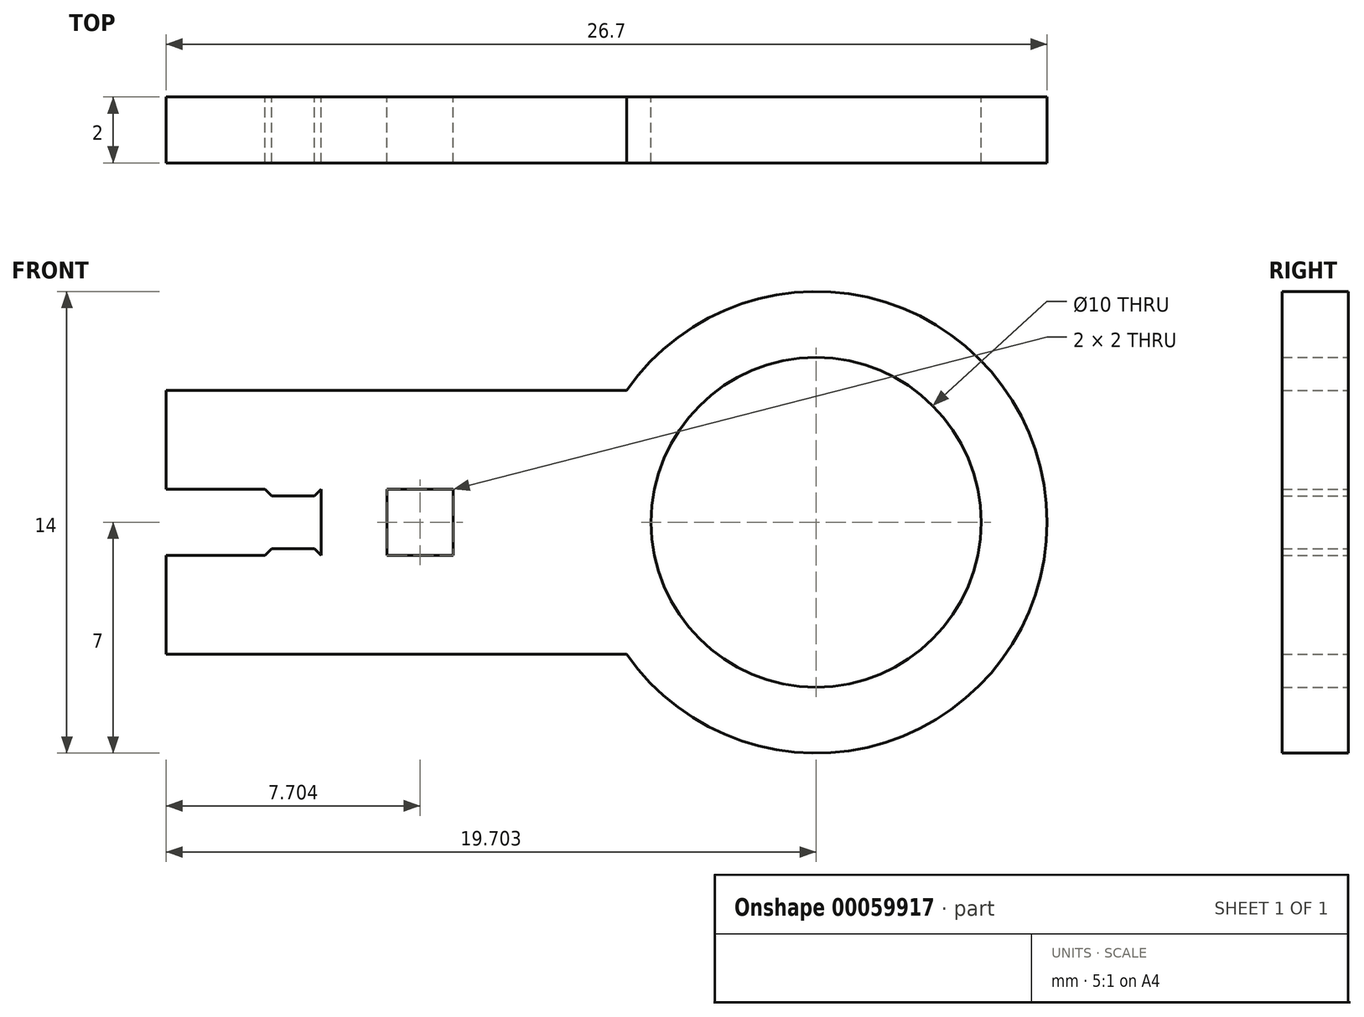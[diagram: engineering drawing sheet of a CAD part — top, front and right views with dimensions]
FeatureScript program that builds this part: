
annotation { "Feature Type Name" : "Feature", "Feature Type Description" : "" }
export const myFeature = defineFeature(function(context is Context, id is Id, definition is map)
    precondition{}
    {
        {
            var Q0;
            Q0=qCreatedBy(makeId("Front.planeOp"),FACE);
            var sketch = newSketch(context, id + "F0", { "sketchPlane" : qUnion([Q0])});
            skCircle(sketch, "E0", {"center": v(24.7, 0) * mm, "radius": 5 * mm});
            skCircle(sketch, "E1.0", {"center": v(24.7, 0) * mm, "radius": 7 * mm});
            skLineSegment(sketch, "E2.0", {"start": v(18.96, 4) * mm, "end": v(5, 4) * mm});
            skLineSegment(sketch, "E3.0", {"start": v(17.78, 1) * mm, "end": v(5, 1) * mm});
            skLineSegment(sketch, "E4", {"start": v(13.7, 1) * mm, "end": v(13.7, -1) * mm});
            skLineSegment(sketch, "E5", {"start": v(11.7, 1) * mm, "end": v(11.7, -1) * mm});
            skLineSegment(sketch, "E6", {"start": v(9.7, 1) * mm, "end": v(9.7, 0) * mm});
            skLineSegment(sketch, "E7", {"start": v(8.2, 0.8) * mm, "end": v(8, 1) * mm});
            skLineSegment(sketch, "E8", {"start": v(8, 1) * mm, "end": v(8, 4) * mm});
            skLineSegment(sketch, "E9", {"start": v(5, 4) * mm, "end": v(5, 1) * mm});
            skLineSegment(sketch, "E10", {"start": v(9.7, 1) * mm, "end": v(9.5, 0.8) * mm});
            skLineSegment(sketch, "E11", {"start": v(9.5, 0.8) * mm, "end": v(8.2, 0.8) * mm});
            skLineSegment(sketch, "E12.MirrorCS", {"start": v(9.7, -1) * mm, "end": v(9.5, -0.8) * mm});
            skLineSegment(sketch, "E13.MirrorCS", {"start": v(8.2, -0.8) * mm, "end": v(8, -1) * mm});
            skLineSegment(sketch, "E14.MirrorCS", {"start": v(5, -4) * mm, "end": v(5, -1) * mm});
            skLineSegment(sketch, "E15.MirrorCS", {"start": v(9.5, -0.8) * mm, "end": v(8.2, -0.8) * mm});
            skLineSegment(sketch, "E16.MirrorCS", {"start": v(17.78, -1) * mm, "end": v(5, -1) * mm});
            skLineSegment(sketch, "E17.MirrorCS", {"start": v(8, -1) * mm, "end": v(8, -4) * mm});
            skLineSegment(sketch, "E18.MirrorCS", {"start": v(18.96, -4) * mm, "end": v(5, -4) * mm});
            skLineSegment(sketch, "E19.MirrorCS", {"start": v(9.7, -1) * mm, "end": v(9.7, 0) * mm});
            skPoint(sketch, "E20.orphan", {"position": v(13.7, 0) * mm});
            skPoint(sketch, "E21.MirrorCS.end.orphan", {"position": v(11.7, 0) * mm});
            skPoint(sketch, "E21.MirrorCS.start.orphan", {"position": v(11.7, -1) * mm});
            skSolve(sketch);
        }
        {
            var Q0;
            Q0=makeQuery(id+"F0.imprint","IMPRINT",FACE,{"disambiguationData":[TD([[makeQuery(id+"F0.imprint","IMPRINT",EDGE,{"derivedFrom":sQuery(id+"F0.wireOp",EDGE,"E0")}),-1.0]])]});
            var Q1;
            {var subQ7=sQuery(id+"F0.wireOp",EDGE,"E8");Q1=makeQuery(id+"F0.imprint","IMPRINT",FACE,{"disambiguationData":[TD([[makeQuery(id+"F0.imprint","IMPRINT",EDGE,{"derivedFrom":subQ7}),-1.0]])]});}
            var Q2;
            {var subQ5=sQuery(id+"F0.wireOp",EDGE,"E4");Q2=makeQuery(id+"F0.imprint","IMPRINT",FACE,{"disambiguationData":[TD([[makeQuery(id+"F0.imprint","IMPRINT",EDGE,{"derivedFrom":subQ5}),1.0]])]});}
            var Q3;
            {var subQ0=sQuery(id+"F0.wireOp",EDGE,"E5");Q3=makeQuery(id+"F0.imprint","IMPRINT",FACE,{"disambiguationData":[TD([[makeQuery(id+"F0.imprint","IMPRINT",EDGE,{"derivedFrom":subQ0}),-1.0]])]});}
            var Q4;
            {var subQ8=sQuery(id+"F0.wireOp",EDGE,"E17.MirrorCS");Q4=makeQuery(id+"F0.imprint","IMPRINT",FACE,{"disambiguationData":[TD([[makeQuery(id+"F0.imprint","IMPRINT",EDGE,{"derivedFrom":subQ8}),1.0]])]});}
            var Q5;
            {var subQ0=sQuery(id+"F0.wireOp",EDGE,"E12.MirrorCS");Q5=makeQuery(id+"F0.imprint","IMPRINT",FACE,{"disambiguationData":[TD([[makeQuery(id+"F0.imprint","IMPRINT",EDGE,{"derivedFrom":subQ0}),1.0]])]});}
            var Q6;
            {var subQ2=sQuery(id+"F0.wireOp",EDGE,"E7");Q6=makeQuery(id+"F0.imprint","IMPRINT",FACE,{"disambiguationData":[TD([[makeQuery(id+"F0.imprint","IMPRINT",EDGE,{"derivedFrom":subQ2}),-1.0]])]});}
            var Q7;
            {var subQ2=sQuery(id+"F0.wireOp",EDGE,"E8");Q7=makeQuery(id+"F0.imprint","IMPRINT",FACE,{"disambiguationData":[TD([[makeQuery(id+"F0.imprint","IMPRINT",EDGE,{"derivedFrom":subQ2}),1.0]])]});}
            var Q8;
            {var subQ0=sQuery(id+"F0.wireOp",EDGE,"E14.MirrorCS");Q8=makeQuery(id+"F0.imprint","IMPRINT",FACE,{"disambiguationData":[TD([[makeQuery(id+"F0.imprint","IMPRINT",EDGE,{"derivedFrom":subQ0}),-1.0]])]});}
            extrude(context, id + "F1", {"entities" : qUnion([Q0, Q1, Q2, Q3, Q4, Q5, Q6, Q7, Q8]), "depth" : 2 * mm});
        }
    });
